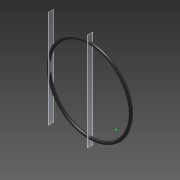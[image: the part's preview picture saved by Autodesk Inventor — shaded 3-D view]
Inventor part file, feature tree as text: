
AUTODESK INVENTOR PART (.ipt)
format: ipt  version: 2015 (Build 190159000, 159)  size: 144,896 bytes
history: native  units: mm
features: other x3, sketch x2, revolve x1, hole x1
ambient origin geometry x8: Origin, YZ Plane, XZ Plane, XY Plane, X Axis, Y Axis, Z Axis, Center Point
bodies: Body1 (feature_tree)
feature tree (7):
  other  "Bryła1"
  revolve  "Obrót1"
  other  "Płaszczyzna do otworu na wentyl 1"
  other  "Płaszczyzna do otworu na wentyl 1.1"
  hole  "Otwór na wentyl"  [1 undecoded]
  sketch  "Szkic1"
  sketch  "Szkic4"
note: 1 required parameter value undecoded (feature->parameter linkage not recoverable at this tier; creation-order binding heuristic only, values carry confidence <= 0.55)
